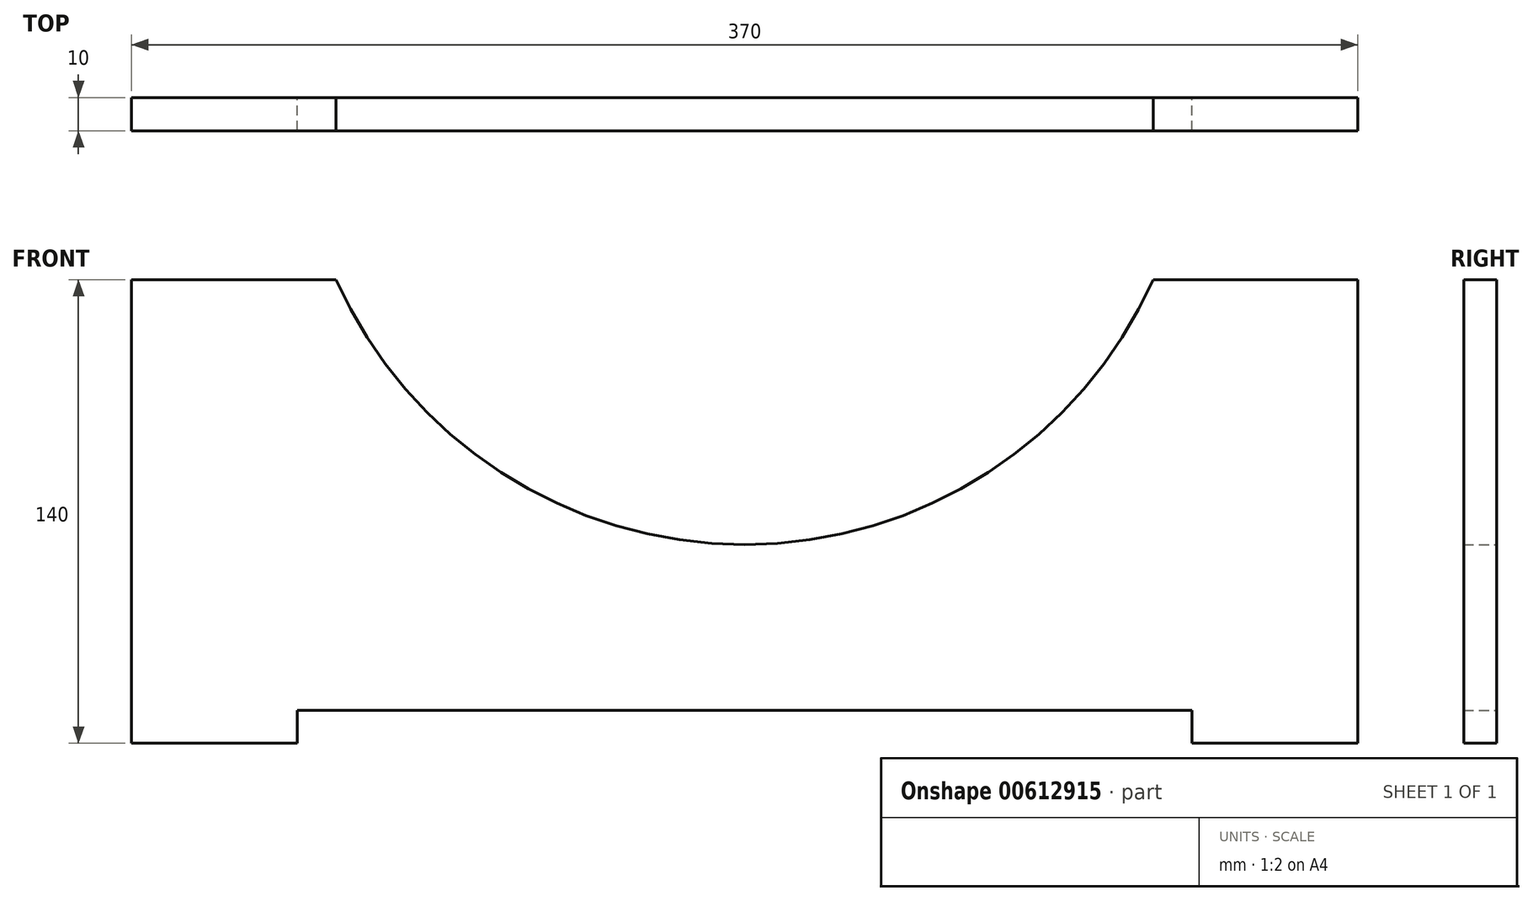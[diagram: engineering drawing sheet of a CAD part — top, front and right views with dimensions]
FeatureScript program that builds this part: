
annotation { "Feature Type Name" : "Feature", "Feature Type Description" : "" }
export const myFeature = defineFeature(function(context is Context, id is Id, definition is map)
    precondition{}
    {
        {
            var Q0;
            Q0=qCreatedBy(makeId("Front.planeOp"),FACE);
            var sketch = newSketch(context, id + "F0", { "sketchPlane" : qUnion([Q0])});
            skLineSegment(sketch, "E0", {"start": v(135, 0) * mm, "end": v(185, 0) * mm});
            skLineSegment(sketch, "E1", {"start": v(-135, 0) * mm, "end": v(-185, 0) * mm});
            skLineSegment(sketch, "E2", {"start": v(0, 0) * mm, "end": v(0, 10) * mm});
            skArc(sketch, "E3", {"start": v(-123.29, 140) * mm, "mid": v(0, 60) * mm, "end": v(123.29, 140) * mm});
            skLineSegment(sketch, "E4", {"start": v(-123.29, 140) * mm, "end": v(-185, 140) * mm});
            skLineSegment(sketch, "E5", {"start": v(-185, 140) * mm, "end": v(-185, 0) * mm});
            skLineSegment(sketch, "E6", {"start": v(123.29, 140) * mm, "end": v(185, 140) * mm});
            skLineSegment(sketch, "E7", {"start": v(185, 0) * mm, "end": v(185, 140) * mm});
            skLineSegment(sketch, "E8", {"start": v(-185, 0) * mm, "end": v(-135, 0) * mm});
            skLineSegment(sketch, "E9", {"start": v(-135, 0) * mm, "end": v(-135, 10) * mm});
            skLineSegment(sketch, "E10", {"start": v(-135, 10) * mm, "end": v(135, 10) * mm});
            skLineSegment(sketch, "E11", {"start": v(185, 0) * mm, "end": v(135, 0) * mm});
            skLineSegment(sketch, "E12", {"start": v(135, 10) * mm, "end": v(135, 0) * mm});
            skLineSegment(sketch, "E13", {"start": v(0, 0) * mm, "end": v(0, 60) * mm});
            skLineSegment(sketch, "E14", {"start": v(0, 60) * mm, "end": v(-123.29, 140) * mm});
            skSolve(sketch);
        }
        {
            var Q0;
            Q0=makeQuery(id+"F0.imprint","IMPRINT",FACE,{"disambiguationData":[TD([[makeQuery(id+"F0.imprint","IMPRINT",EDGE,{"derivedFrom":sQuery(id+"F0.wireOp",EDGE,"E3")}),-1.0]])]});
            extrude(context, id + "F1", {"entities" : qUnion([Q0]), "depth" : 10 * mm, "offsetDistance" : 25 * mm});
        }
    });
